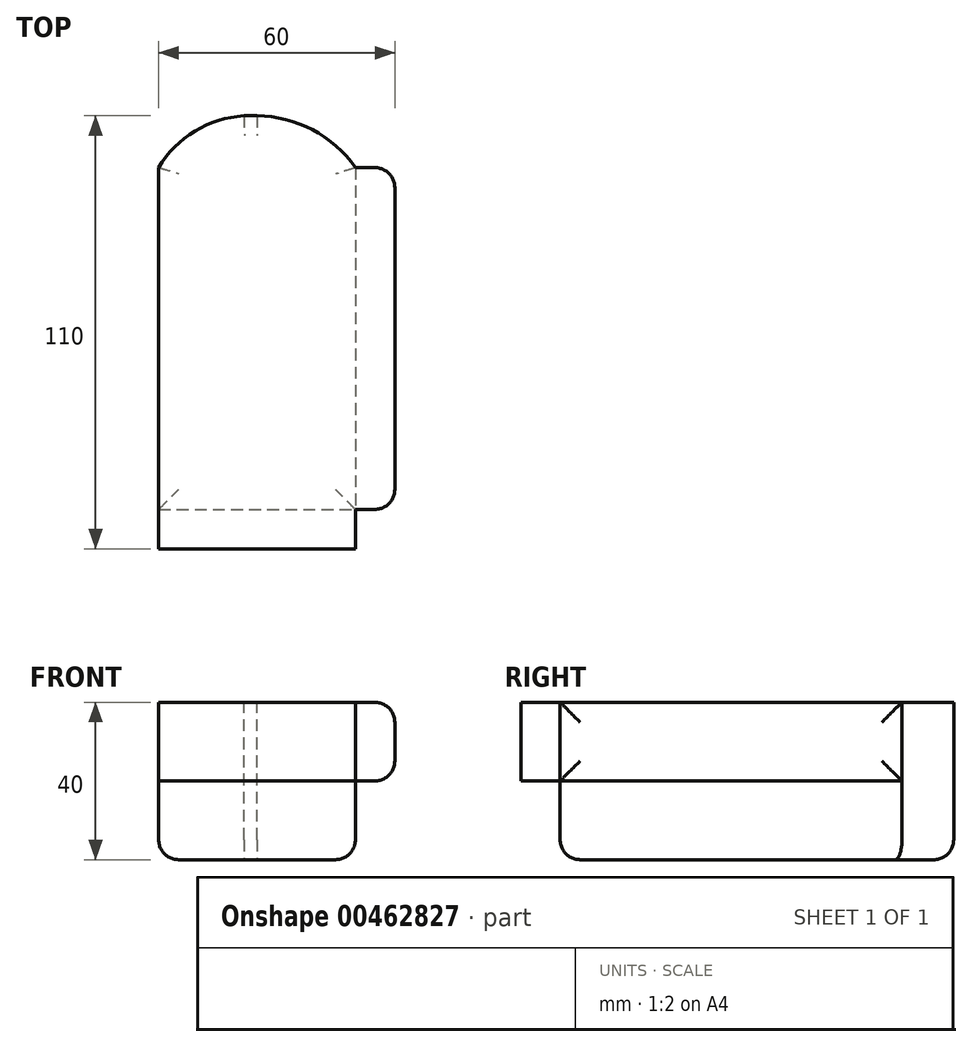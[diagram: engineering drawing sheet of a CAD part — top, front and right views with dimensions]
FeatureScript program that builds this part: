
annotation { "Feature Type Name" : "Feature", "Feature Type Description" : "" }
export const myFeature = defineFeature(function(context is Context, id is Id, definition is map)
    precondition{}
    {
        {
            var Q0;
            Q0=qCreatedBy(makeId("Top.planeOp"),FACE);
            var sketch = newSketch(context, id + "F0", { "sketchPlane" : qUnion([Q0])});
            skLineSegment(sketch, "E0.bottom", {"start": v(-22.2, 65.18) * mm, "end": v(27.8, 65.18) * mm});
            skLineSegment(sketch, "E0.top", {"start": v(-22.2, -34.82) * mm, "end": v(27.8, -34.82) * mm});
            skLineSegment(sketch, "E0.left", {"start": v(-22.2, 65.18) * mm, "end": v(-22.2, -34.82) * mm});
            skLineSegment(sketch, "E0.right", {"start": v(27.8, 65.18) * mm, "end": v(27.8, -34.82) * mm});
            skSolve(sketch);
        }
        {
            var Q0;
            Q0=makeQuery(id+"F0.imprint","IMPRINT",FACE,{"disambiguationData":[TD([[makeQuery(id+"F0.imprint","IMPRINT",EDGE,{"derivedFrom":sQuery(id+"F0.wireOp",EDGE,"E0.bottom")}),-1.0]])]});
            var Q1;
            Q1 = qSketchRegion(id + "F0", true);
            extrude(context, id + "F1", {"entities" : qUnion([Q0, Q1]), "depth" : 40 * mm});
        }
        {
            var Q0;
            Q0=makeQuery(id+"F1.opExtrude","CAP_FACE",FACE,{"disambiguationData":[OSD([sQuery(id+"F0.wireOp",EDGE,"E0.bottom"),sQuery(id+"F0.wireOp",EDGE,"E0.top"),sQuery(id+"F0.wireOp",EDGE,"E0.left"),sQuery(id+"F0.wireOp",EDGE,"E0.right")])],"isStart":false});
            var sketch = newSketch(context, id + "F2", { "sketchPlane" : qUnion([Q0])});
            skArc(sketch, "E1", {"start": v(2.8, 65.18) * mm, "mid": v(-11.54, 62.1) * mm, "end": v(-22.2, 52.02) * mm});
            skArc(sketch, "E2", {"start": v(27.8, 52.02) * mm, "mid": v(16.9, 61.62) * mm, "end": v(2.8, 65.18) * mm});
            skSolve(sketch);
        }
        {
            var Q0;
            {var subQ0=sQuery(id+"F2.wireOp",EDGE,"E1");var subQ1=makeQuery(id+"F1.opExtrude","CAP_EDGE",EDGE,{"disambiguationData":[OSD([sQuery(id+"F0.wireOp",EDGE,"E0.left")])],"isStart":false});var subQ2=makeQuery(id+"F2.imprint","INTERSECT",VERTEX,{"derivedFrom":[subQ1,subQ0]});Q0=makeQuery(id+"F2.imprint","IMPRINT",FACE,{"disambiguationData":[TD([[makeQuery(id+"F2.imprint","IMPRINT",EDGE,{"disambiguationData":[TD([[subQ2,1.0]])],"derivedFrom":subQ0}),-1.0]])]});}
            var Q1;
            {var subQ0=sQuery(id+"F2.wireOp",EDGE,"E2");Q1=makeQuery(id+"F2.imprint","IMPRINT",FACE,{"disambiguationData":[TD([[makeQuery(id+"F2.imprint","IMPRINT",EDGE,{"derivedFrom":subQ0}),-1.0]])]});}
            extrude(context, id + "F3", {"entities" : qUnion([Q0, Q1]), "operationType" : NewBodyOperationType.REMOVE, "oppositeDirection" : true, "depth" : 152.4 * mm});
        }
        {
            var Q0;
            Q0=makeQuery(id+"F1.opExtrude","SWEPT_FACE",FACE,{"disambiguationData":[OSD([sQuery(id+"F0.wireOp",EDGE,"E0.right")])]});
            var sketch = newSketch(context, id + "F4", { "sketchPlane" : qUnion([Q0])});
            skLineSegment(sketch, "E3", {"start": v(-34.82, 20) * mm, "end": v(52.02, 20) * mm});
            skSolve(sketch);
        }
        {
            var Q0;
            Q0=makeQuery(id+"F1.opExtrude","SWEPT_FACE",FACE,{"disambiguationData":[OSD([sQuery(id+"F0.wireOp",EDGE,"E0.left")])]});
            var sketch = newSketch(context, id + "F5", { "sketchPlane" : qUnion([Q0])});
            skLineSegment(sketch, "E4", {"start": v(-52.02, 20) * mm, "end": v(34.82, 20) * mm});
            skSolve(sketch);
        }
        {
            var Q0;
            Q0=makeQuery(id+"F1.opExtrude","SWEPT_FACE",FACE,{"disambiguationData":[OSD([sQuery(id+"F0.wireOp",EDGE,"E0.top")])]});
            var sketch = newSketch(context, id + "F6", { "sketchPlane" : qUnion([Q0])});
            skLineSegment(sketch, "E5", {"start": v(-22.2, 20) * mm, "end": v(27.8, 20) * mm});
            skSolve(sketch);
        }
        {
            var Q0;
            {var subQ0=sQuery(id+"F4.wireOp",EDGE,"E3");Q0=makeQuery(id+"F4.imprint","IMPRINT",FACE,{"disambiguationData":[TD([[makeQuery(id+"F4.imprint","IMPRINT",EDGE,{"derivedFrom":subQ0}),1.0]])]});}
            var Q1;
            {var subQ0=sQuery(id+"F5.wireOp",EDGE,"E4");Q1=makeQuery(id+"F5.imprint","IMPRINT",FACE,{"disambiguationData":[TD([[makeQuery(id+"F5.imprint","IMPRINT",EDGE,{"derivedFrom":subQ0}),1.0]])]});}
            extrude(context, id + "F7", {"entities" : qUnion([Q0, Q1]), "operationType" : NewBodyOperationType.ADD, "depth" : 10 * mm});
        }
        {
            var Q0;
            Q0=makeQuery(id+"F7.opExtrude","CAP_EDGE",EDGE,{"disambiguationData":[OSD([sQuery(id+"F4.wireOp",EDGE,"E3")])],"isStart":true});
            var Q1;
            Q1=makeQuery(id+"F3.boolean.opBoolean","COPY",EDGE,{"derivedFrom":makeQuery(id+"F3.opExtrude","CAP_EDGE",EDGE,{"disambiguationData":[OSD([sQuery(id+"F2.wireOp",EDGE,"E2")])],"isStart":true})});
            var Q2;
            Q2=makeQuery(id+"F1.opExtrude","CAP_FACE",FACE,{"disambiguationData":[OSD([sQuery(id+"F0.wireOp",EDGE,"E0.bottom"),sQuery(id+"F0.wireOp",EDGE,"E0.top"),sQuery(id+"F0.wireOp",EDGE,"E0.left"),sQuery(id+"F0.wireOp",EDGE,"E0.right")])],"isStart":true});
            fillet(context, id + "F8", {"entities" : qUnion([Q0, Q1, Q2]), "radius" : 5.08 * mm, "tangentPropagation" : true, "allowEdgeOverflow" : false});
        }
        {
            var Q0;
            Q0=makeQuery(id+"F7.opExtrude","CAP_FACE",FACE,{"disambiguationData":[OSD([sQuery(id+"F0.wireOp",EDGE,"E0.top"),sQuery(id+"F0.wireOp",EDGE,"E0.right"),sQuery(id+"F2.wireOp",EDGE,"E2"),sQuery(id+"F4.wireOp",EDGE,"E3")])],"isStart":false});
            fillet(context, id + "F9", {"entities" : qUnion([Q0]), "radius" : 5.08 * mm, "tangentPropagation" : true, "allowEdgeOverflow" : false});
        }
        {
            var Q0;
            {var subQ0=sQuery(id+"F6.wireOp",EDGE,"E5");Q0=makeQuery(id+"F6.imprint","IMPRINT",FACE,{"disambiguationData":[TD([[makeQuery(id+"F6.imprint","IMPRINT",EDGE,{"derivedFrom":subQ0}),1.0]])]});}
            extrude(context, id + "F10", {"entities" : qUnion([Q0]), "operationType" : NewBodyOperationType.ADD, "depth" : 10 * mm});
        }
    });
